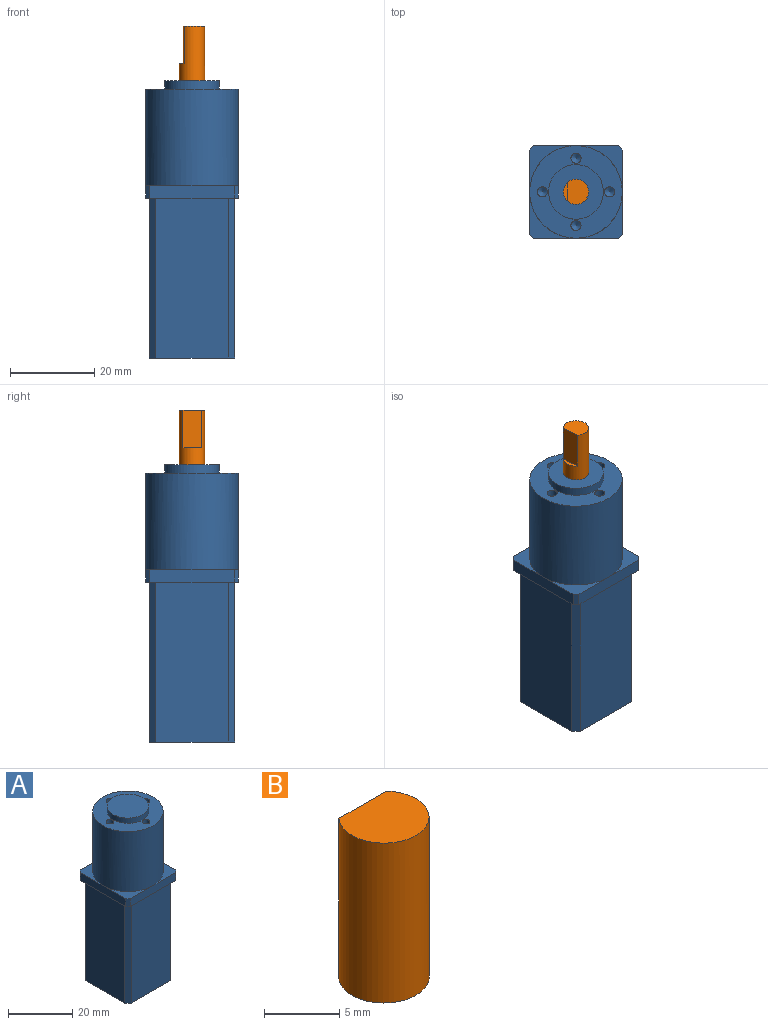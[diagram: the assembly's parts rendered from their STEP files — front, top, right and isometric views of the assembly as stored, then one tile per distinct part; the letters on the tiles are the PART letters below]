
ASSEMBLY  parts=2 mates=1
PART A: 34 faces, bbox 22x22x66 mm
  f0: cone r=0mm half-angle=59deg, axis (0,0,1), area 5.3mm2, adj f1
  f1: cylinder r=1.2mm len=3mm, axis (0,0,1), area 22.6mm2, adj f0,f21
  f2: cone r=0mm half-angle=59deg, axis (0,0,1), area 5.3mm2, adj f3
  f3: cylinder r=1.2mm len=3mm, axis (0,0,1), area 22.6mm2, adj f2,f21
  f4: cone r=0mm half-angle=59deg, axis (0,0,1), area 5.3mm2, adj f5
  f5: cylinder r=1.2mm len=3mm, axis (0,0,1), area 22.6mm2, adj f4,f21
  f6: plane 11x11mm, normal (0,0,1), area 25.5mm2, adj f16,f17,f20,f24
  f7: plane 11x11mm, normal (0,0,1), area 25.5mm2, adj f14,f17,f20,f25
  f8: plane 11x11mm, normal (0,0,1), area 25.5mm2, adj f14,f15,f20,f26
  f9: plane 38x17.3mm, normal (-1,0,0), area 657.4mm2, adj f13,f19,f28,f29
  f10: plane 38x17.3mm, normal (0,-1,0), area 657.4mm2, adj f13,f19,f29,f30
  f11: plane 38x17.3mm, normal (1,0,0), area 657.4mm2, adj f13,f19,f30,f31
  f12: plane 38x17.3mm, normal (0,1,0), area 657.4mm2, adj f13,f19,f28,f31
  f13: plane 20.3x20.3mm, normal (0,0,-1), area 407.6mm2, adj f9,f10,f11,f12,f28,f29,f30,f31
  f14: plane 20x3mm, normal (-1,0,0), area 60mm2, adj f7,f8,f19,f25,f26
  f15: plane 20x3mm, normal (0,-1,0), area 60mm2, adj f8,f18,f19,f26,f27
  f16: plane 20x3mm, normal (1,0,0), area 60mm2, adj f6,f18,f19,f24,f27
  f17: plane 20x3mm, normal (0,1,0), area 60mm2, adj f6,f7,f19,f24,f25
  f18: plane 11x11mm, normal (0,0,1), area 25.5mm2, adj f15,f16,f20,f27
  f19: plane 22x22mm, normal (0,0,-1), area 74.4mm2, adj f9,f10,f11,f12,f14,f15,f16,f17
  f20: cylinder r=11mm len=22.95mm, axis (0,0,-1), area 1586.2mm2, adj f6,f7,f8,f18,f21
  f21: plane 22x22mm, normal (0,0,1), area 229.3mm2, adj f1,f3,f5,f20,f22,f33
  f22: cylinder r=6.5mm len=13mm, axis (0,0,-1), area 81.7mm2, adj f21,f23
  f23: plane 13x13mm, normal (0,0,1), area 132.7mm2, adj f22
  f24: plane 3x1mm, normal (0.71,0.71,0), area 4.2mm2, adj f6,f16,f17,f19
  f25: plane 3x1mm, normal (-0.71,0.71,0), area 4.2mm2, adj f7,f14,f17,f19
  f26: plane 3x1mm, normal (-0.71,-0.71,0), area 4.2mm2, adj f8,f14,f15,f19
  f27: plane 3x1mm, normal (0.71,-0.71,0), area 4.2mm2, adj f15,f16,f18,f19
  f28: plane 38x1.5mm, normal (-0.71,0.71,0), area 80.6mm2, adj f9,f12,f13,f19
  f29: plane 38x1.5mm, normal (-0.71,-0.71,0), area 80.6mm2, adj f9,f10,f13,f19
  f30: plane 38x1.5mm, normal (0.71,-0.71,0), area 80.6mm2, adj f10,f11,f13,f19
  f31: plane 38x1.5mm, normal (0.71,0.71,0), area 80.6mm2, adj f11,f12,f13,f19
  f32: cone r=0mm half-angle=59deg, axis (0,0,1), area 5.3mm2, adj f33
  f33: cylinder r=1.2mm len=3mm, axis (0,0,1), area 22.6mm2, adj f21,f32
PART B: 5 faces, bbox 6x6x13 mm
  f0: cylinder r=3mm len=13mm, axis (0,0,-1), area 199.6mm2, adj f1,f2,f3,f4
  f1: plane 6x5mm, normal (0,0,1), area 25.2mm2, adj f0,f3
  f2: plane 6x6mm, normal (0,0,-1), area 28.3mm2, adj f0
  f3: plane 9x4.47mm, normal (0,1,0), area 40.2mm2, adj f0,f1,f4
  f4: plane 4.47x1mm, normal (0,0,1), area 3.1mm2, adj f0,f3
PLACE A at identity fixed
PLACE B rot(axis=(0,0,1),92.5deg) t=(0,0,0)mm
MATE revolute A.f22 <-> B.f0  axis (0,0,1) through (0,0,65.95)mm
